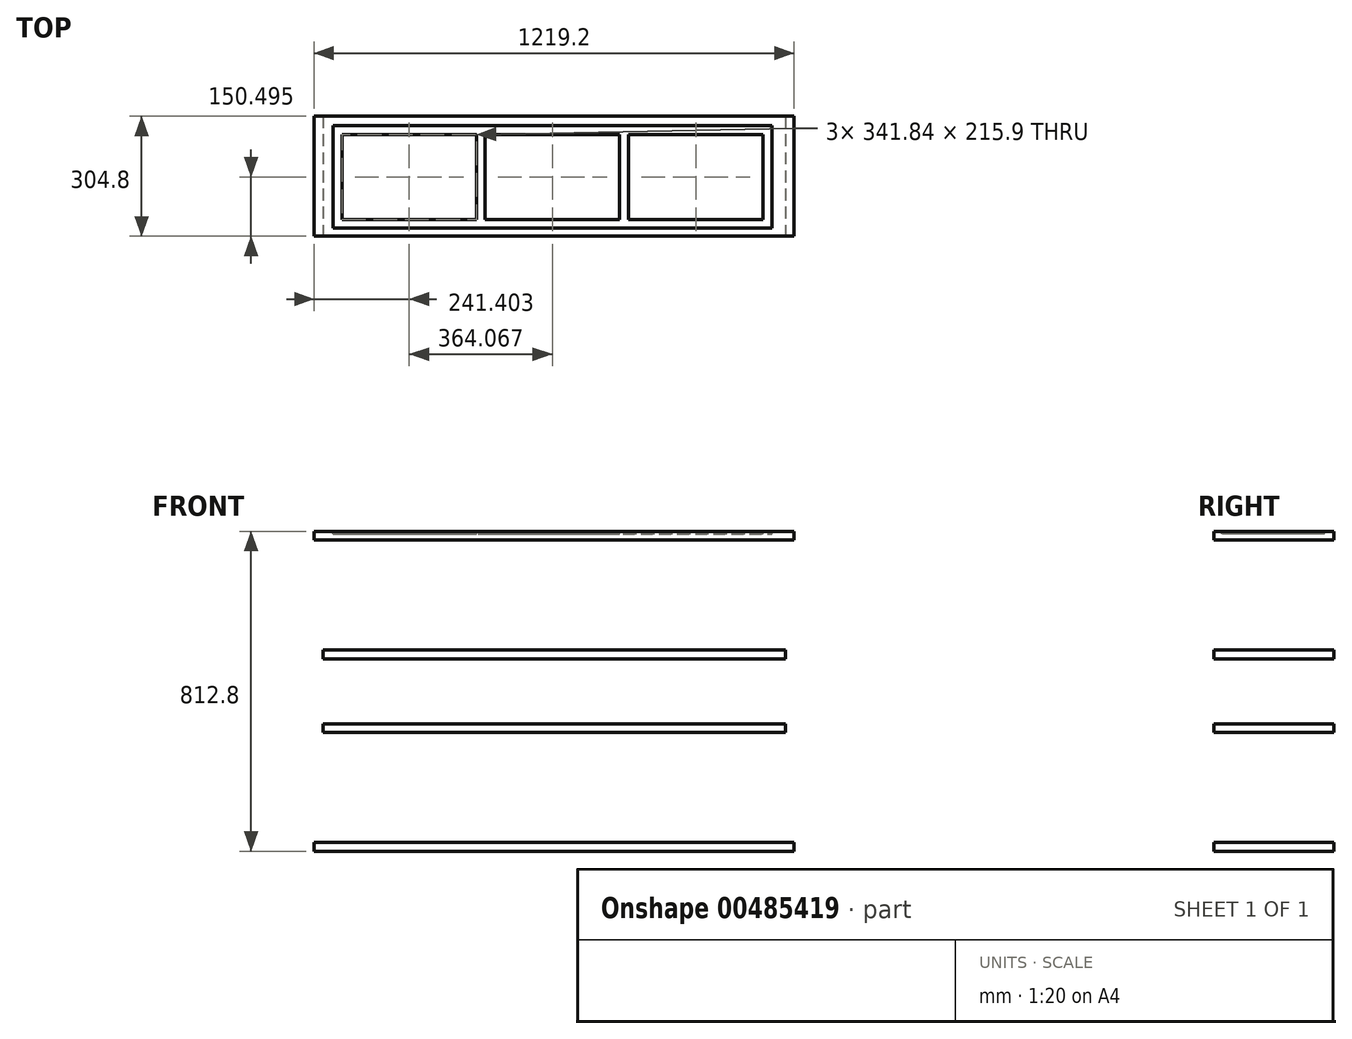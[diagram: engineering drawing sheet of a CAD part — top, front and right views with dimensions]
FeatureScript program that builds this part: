
annotation { "Feature Type Name" : "Feature", "Feature Type Description" : "" }
export const myFeature = defineFeature(function(context is Context, id is Id, definition is map)
    precondition{}
    {
        {
            var Q0;
            Q0=qCreatedBy(makeId("Front.planeOp"),FACE);
            var sketch = newSketch(context, id + "F0", { "sketchPlane" : qUnion([Q0])});
            skLineSegment(sketch, "E0.bottom", {"start": v(600.5, -437.81) * mm, "end": v(-618.7, -437.81) * mm});
            skLineSegment(sketch, "E0.top", {"start": v(600.5, -460.04) * mm, "end": v(-618.7, -460.04) * mm});
            skLineSegment(sketch, "E0.left", {"start": v(600.5, -437.81) * mm, "end": v(600.5, -460.04) * mm});
            skLineSegment(sketch, "E0.right", {"start": v(-618.7, -437.81) * mm, "end": v(-618.7, -460.04) * mm});
            skLineSegment(sketch, "E1.bottom", {"start": v(600.5, -437.81) * mm, "end": v(578.28, -437.81) * mm});
            skLineSegment(sketch, "E1.top", {"start": v(600.5, 352.76) * mm, "end": v(578.28, 352.76) * mm});
            skLineSegment(sketch, "E1.left", {"start": v(600.5, -437.81) * mm, "end": v(600.5, 352.76) * mm});
            skLineSegment(sketch, "E1.right", {"start": v(578.28, -437.81) * mm, "end": v(578.28, 330.54) * mm});
            skLineSegment(sketch, "E2.bottom", {"start": v(-618.7, -437.81) * mm, "end": v(-596.47, -437.81) * mm});
            skLineSegment(sketch, "E2.top", {"start": v(-618.7, 352.76) * mm, "end": v(-596.47, 352.76) * mm});
            skLineSegment(sketch, "E2.left", {"start": v(-618.7, -437.81) * mm, "end": v(-618.7, 352.76) * mm});
            skLineSegment(sketch, "E2.right", {"start": v(-596.47, -437.81) * mm, "end": v(-596.47, 330.54) * mm});
            skLineSegment(sketch, "E3.bottom", {"start": v(578.28, -136.19) * mm, "end": v(-558.37, -136.19) * mm});
            skLineSegment(sketch, "E3.top", {"start": v(578.28, -158.41) * mm, "end": v(-558.37, -158.41) * mm});
            skLineSegment(sketch, "E3.left", {"start": v(578.28, -136.19) * mm, "end": v(578.28, -158.41) * mm});
            skLineSegment(sketch, "E4.bottom", {"start": v(-596.47, 28.91) * mm, "end": v(540.18, 28.91) * mm});
            skLineSegment(sketch, "E4.top", {"start": v(-596.47, 51.14) * mm, "end": v(540.18, 51.14) * mm});
            skLineSegment(sketch, "E4.left", {"start": v(-596.47, 28.91) * mm, "end": v(-596.47, 51.14) * mm});
            skLineSegment(sketch, "E5.bottom", {"start": v(578.28, 352.76) * mm, "end": v(-558.37, 352.76) * mm});
            skLineSegment(sketch, "E5.top", {"start": v(578.28, 330.54) * mm, "end": v(-558.37, 330.54) * mm});
            skLineSegment(sketch, "E6.bottom", {"start": v(-558.37, -136.19) * mm, "end": v(-596.47, -136.19) * mm});
            skLineSegment(sketch, "E6.top", {"start": v(-558.37, -158.41) * mm, "end": v(-596.47, -158.41) * mm});
            skLineSegment(sketch, "E7.bottom", {"start": v(540.18, 51.14) * mm, "end": v(578.28, 51.14) * mm});
            skLineSegment(sketch, "E7.top", {"start": v(540.18, 28.91) * mm, "end": v(578.28, 28.91) * mm});
            skLineSegment(sketch, "E8.bottom", {"start": v(-558.37, 352.76) * mm, "end": v(-596.47, 352.76) * mm});
            skLineSegment(sketch, "E8.top", {"start": v(-558.37, 330.54) * mm, "end": v(-596.47, 330.54) * mm});
            skLineSegment(sketch, "E9", {"start": v(-596.47, 330.54) * mm, "end": v(-618.7, 330.54) * mm});
            skLineSegment(sketch, "E10", {"start": v(578.28, 330.54) * mm, "end": v(600.5, 330.54) * mm});
            skSolve(sketch);
        }
        {
            var Q0;
            {var subQ3=sQuery(id+"F0.wireOp",EDGE,"E1.top");Q0=makeQuery(id+"F0.imprint","IMPRINT",FACE,{"disambiguationData":[TD([[makeQuery(id+"F0.imprint","IMPRINT",EDGE,{"derivedFrom":subQ3}),1.0]])]});}
            var Q1;
            {var subQ1=sQuery(id+"F0.wireOp",EDGE,"E2.bottom");Q1=makeQuery(id+"F0.imprint","IMPRINT",FACE,{"disambiguationData":[TD([[makeQuery(id+"F0.imprint","IMPRINT",EDGE,{"derivedFrom":subQ1}),1.0]])]});}
            var Q2;
            {var subQ1=sQuery(id+"F0.wireOp",EDGE,"E1.bottom");Q2=makeQuery(id+"F0.imprint","IMPRINT",FACE,{"disambiguationData":[TD([[makeQuery(id+"F0.imprint","IMPRINT",EDGE,{"derivedFrom":subQ1}),-1.0]])]});}
            var Q3;
            Q3=makeQuery(id+"F0.imprint","IMPRINT",FACE,{"disambiguationData":[TD([[makeQuery(id+"F0.imprint","IMPRINT",EDGE,{"derivedFrom":sQuery(id+"F0.wireOp",EDGE,"E4.bottom")}),1.0]])]});
            var Q4;
            Q4=makeQuery(id+"F0.imprint","IMPRINT",FACE,{"disambiguationData":[TD([[makeQuery(id+"F0.imprint","IMPRINT",EDGE,{"derivedFrom":sQuery(id+"F0.wireOp",EDGE,"E3.bottom")}),1.0]])]});
            var Q5;
            Q5=makeQuery(id+"F0.imprint","IMPRINT",FACE,{"disambiguationData":[TD([[makeQuery(id+"F0.imprint","IMPRINT",EDGE,{"derivedFrom":sQuery(id+"F0.wireOp",EDGE,"E0.bottom")}),1.0]])]});
            extrude(context, id + "F1", {"entities" : qUnion([Q0, Q1, Q2, Q3, Q4, Q5]), "oppositeDirection" : true, "depth" : 304.8 * mm});
        }
        {
            var Q0;
            Q0=makeQuery(id+"F1.opExtrude","SWEPT_FACE",FACE,{"disambiguationData":[OSD([sQuery(id+"F0.wireOp",EDGE,"E1.top"),sQuery(id+"F0.wireOp",EDGE,"E2.top"),sQuery(id+"F0.wireOp",EDGE,"E5.bottom"),sQuery(id+"F0.wireOp",EDGE,"E8.bottom")])]});
            var sketch = newSketch(context, id + "F2", { "sketchPlane" : qUnion([Q0])});
            skLineSegment(sketch, "E11.0", {"start": v(-570.43, 20.32) * mm, "end": v(544, 20.32) * mm});
            skLineSegment(sketch, "E11.1", {"start": v(-570.43, 280.67) * mm, "end": v(-570.43, 20.32) * mm});
            skLineSegment(sketch, "E11.2", {"start": v(544, 280.67) * mm, "end": v(-570.43, 280.67) * mm});
            skLineSegment(sketch, "E11.3", {"start": v(544, 20.32) * mm, "end": v(544, 280.67) * mm});
            skLineSegment(sketch, "E12.0", {"start": v(521.77, 258.45) * mm, "end": v(179.93, 258.45) * mm});
            skLineSegment(sketch, "E12.1", {"start": v(521.77, 42.55) * mm, "end": v(521.77, 258.45) * mm});
            skLineSegment(sketch, "E12.2", {"start": v(-548.2, 42.55) * mm, "end": v(-206.37, 42.55) * mm});
            skLineSegment(sketch, "E12.3", {"start": v(-548.2, 258.45) * mm, "end": v(-548.2, 42.55) * mm});
            skLineSegment(sketch, "E13", {"start": v(-206.37, 258.45) * mm, "end": v(-206.37, 42.55) * mm});
            skLineSegment(sketch, "E14", {"start": v(-184.14, 258.45) * mm, "end": v(-184.14, 42.55) * mm});
            skLineSegment(sketch, "E15", {"start": v(157.7, 258.45) * mm, "end": v(157.7, 42.55) * mm});
            skLineSegment(sketch, "E16", {"start": v(179.93, 258.45) * mm, "end": v(179.93, 42.55) * mm});
            skLineSegment(sketch, "E17.trimOffspring", {"start": v(-206.37, 258.45) * mm, "end": v(-548.2, 258.45) * mm});
            skLineSegment(sketch, "E18.trimOffspring", {"start": v(-184.14, 42.55) * mm, "end": v(157.7, 42.55) * mm});
            skLineSegment(sketch, "E19.trimOffspring", {"start": v(179.93, 42.55) * mm, "end": v(521.77, 42.55) * mm});
            skLineSegment(sketch, "E20.trimOffspring", {"start": v(157.7, 258.45) * mm, "end": v(-184.14, 258.45) * mm});
            skSolve(sketch);
        }
        {
            var Q0;
            Q0=makeQuery(id+"F2.imprint","IMPRINT",FACE,{"disambiguationData":[TD([[makeQuery(id+"F2.imprint","IMPRINT",EDGE,{"derivedFrom":sQuery(id+"F2.wireOp",EDGE,"E11.0")}),1.0]])]});
            extrude(context, id + "F3", {"entities" : qUnion([Q0]), "operationType" : NewBodyOperationType.REMOVE, "oppositeDirection" : true, "depth" : 6.35 * mm});
        }
        {
            var Q0;
            Q0=makeQuery(id+"F2.imprint","IMPRINT",FACE,{"disambiguationData":[TD([[makeQuery(id+"F2.imprint","IMPRINT",EDGE,{"derivedFrom":sQuery(id+"F2.wireOp",EDGE,"E11.0")}),1.0]])]});
            extrude(context, id + "F4", {"entities" : qUnion([Q0]), "oppositeDirection" : true, "depth" : 6.35 * mm});
        }
    });
